# Revit family: revitupgrade
name_source: partatom
category: Furniture
units: mm (PartAtom-declared; Revit-internal decimal feet)

## family parameters
Always vertical = Yes
Cut with Voids When Loaded = No
Enable Cutting in Views = No
OmniClass Number = 23.40.70.14.64.11
OmniClass Title = Office Furniture
Render Appearance Source = Family Geometry
Room Calculation Point = No
Shared = No
Work Plane-Based = No

## types (9) — shared parameters
Arm = Steelcase - 6205 Black
Assembly Code = E2020200
Base = Steelcase - 4799 Platinum Metallic
Caster = Yes
Default Elevation = 0.00 mm
Description = Think is the chair with a brain and a conscience. It's intelligent enough to understand how you sit and adjust itself intuitively.
Frame = Steelcase - 6205 Black
Glide = No
Headrest Pad = Steelcase - L112 Ebony
Manufacturer = Steelcase
Release Date = October 2024
Style Number(s) = 465A300,465A000,465A300CN,465A000CN
URL = https://www.steelcase.com

## per-type parameters (varying)
| type | Coat Hanger | Fixed Arm | HWPD Arm | Headrest |
| Fixed Arm/Coat Hanger | Yes | Yes | No | No |
| Armless/Coat Hanger | Yes | No | No | No |
| HWPD Arm/Coat Hanger | Yes | No | Yes | No |
| Fixed Arm/Headrest | No | Yes | No | Yes |
| Armless/Headrest | No | No | No | Yes |
| HWPD Arm/Headrest | No | No | Yes | Yes |
| Armless | No | No | No | No |
| Fixed Arm | No | Yes | No | No |
| HWPD Arm | No | No | Yes | No |

## geometry (parser evidence)
native form markers: Sweep x1
no freeform markers — native parametric forms only
